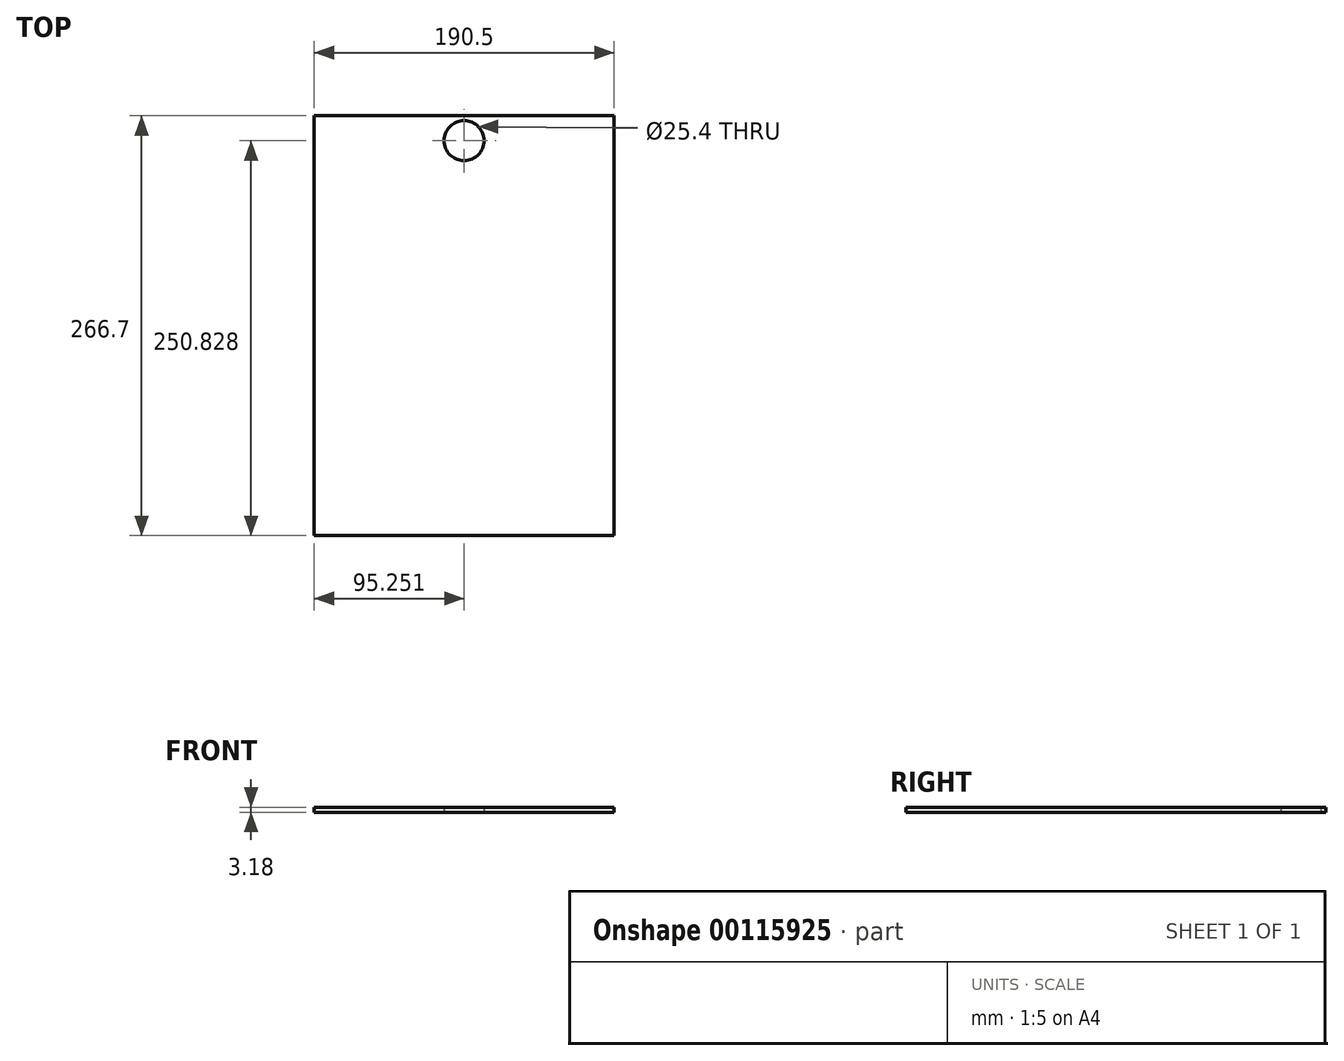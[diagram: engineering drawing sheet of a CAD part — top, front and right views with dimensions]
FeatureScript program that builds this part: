
annotation { "Feature Type Name" : "Feature", "Feature Type Description" : "" }
export const myFeature = defineFeature(function(context is Context, id is Id, definition is map)
    precondition{}
    {
        {
            var Q0;
            Q0=qCreatedBy(makeId("Top.planeOp"),FACE);
            var sketch = newSketch(context, id + "F0", { "sketchPlane" : qUnion([Q0])});
            skLineSegment(sketch, "E0.bottom", {"start": v(82.37, -140.7) * mm, "end": v(-108.13, -140.7) * mm});
            skLineSegment(sketch, "E0.top", {"start": v(82.37, 126) * mm, "end": v(-108.13, 126) * mm});
            skLineSegment(sketch, "E0.left", {"start": v(82.37, -140.7) * mm, "end": v(82.37, 126) * mm});
            skLineSegment(sketch, "E0.right", {"start": v(-108.13, -140.7) * mm, "end": v(-108.13, 126) * mm});
            skCircle(sketch, "E1", {"center": v(-12.88, 110.12) * mm, "radius": 12.7 * mm});
            skSolve(sketch);
        }
        {
            var Q0;
            Q0=makeQuery(id+"F0.imprint","IMPRINT",FACE,{"disambiguationData":[TD([[makeQuery(id+"F0.imprint","IMPRINT",EDGE,{"derivedFrom":sQuery(id+"F0.wireOp",EDGE,"E0.bottom")}),-1.0]])]});
            extrude(context, id + "F1", {"entities" : qUnion([Q0]), "depth" : 3.17 * mm});
        }
    });
